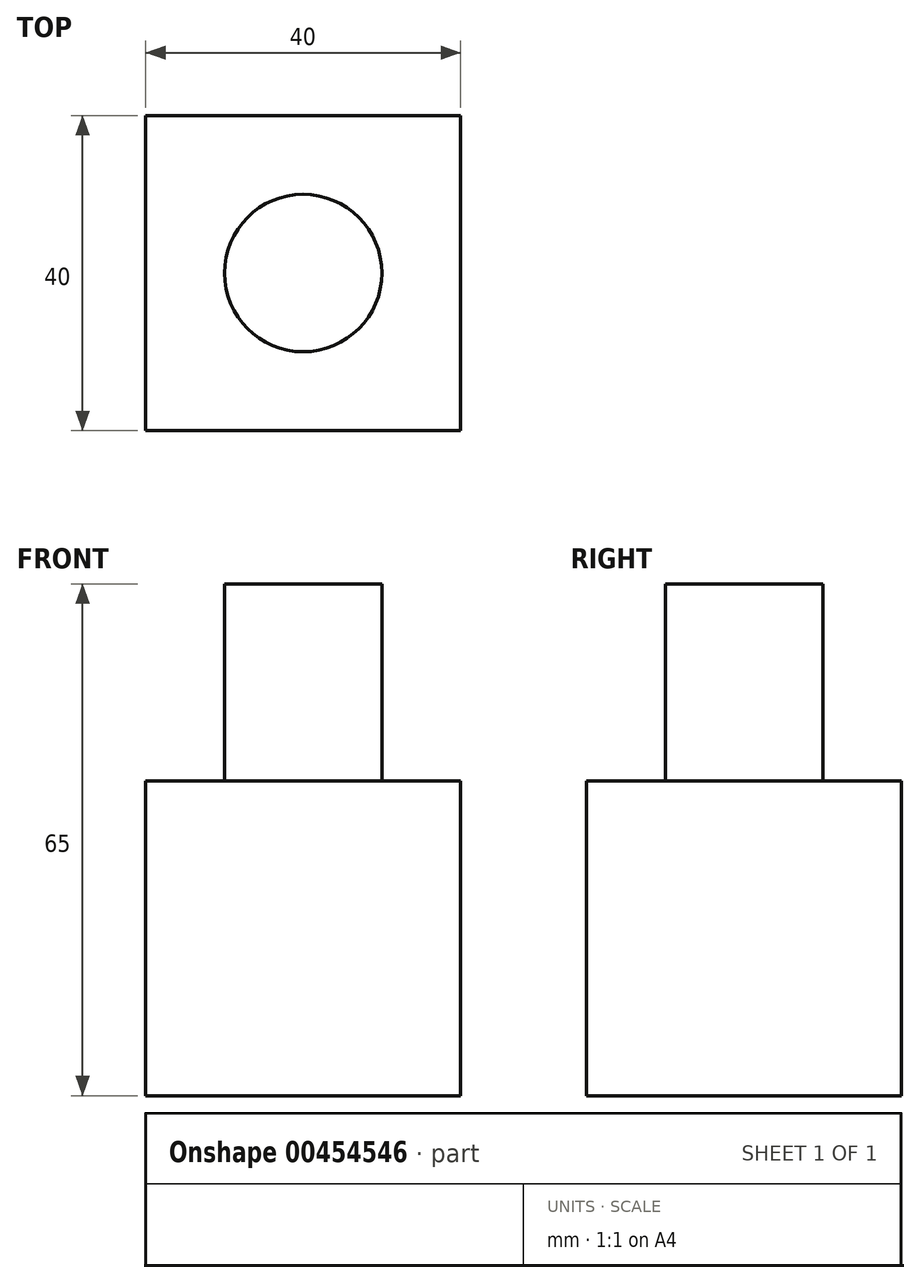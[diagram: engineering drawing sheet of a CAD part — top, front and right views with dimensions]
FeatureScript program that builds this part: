
annotation { "Feature Type Name" : "Feature", "Feature Type Description" : "" }
export const myFeature = defineFeature(function(context is Context, id is Id, definition is map)
    precondition{}
    {
        {
            var Q0;
            Q0=qCreatedBy(makeId("Top.planeOp"),FACE);
            var sketch = newSketch(context, id + "F0", { "sketchPlane" : qUnion([Q0])});
            skLineSegment(sketch, "E0.bottom", {"start": v(-384.05, 0) * mm, "end": v(-344.05, 0) * mm});
            skLineSegment(sketch, "E0.top", {"start": v(-384.05, 40) * mm, "end": v(-344.05, 40) * mm});
            skLineSegment(sketch, "E0.left", {"start": v(-384.05, 0) * mm, "end": v(-384.05, 40) * mm});
            skLineSegment(sketch, "E0.right", {"start": v(-344.05, 0) * mm, "end": v(-344.05, 40) * mm});
            skSolve(sketch);
        }
        {
            var Q0;
            Q0=makeQuery(id+"F0.imprint","IMPRINT",FACE,{"disambiguationData":[TD([[makeQuery(id+"F0.imprint","IMPRINT",EDGE,{"derivedFrom":sQuery(id+"F0.wireOp",EDGE,"E0.bottom")}),1.0]])]});
            extrude(context, id + "F1", {"entities" : qUnion([Q0]), "depth" : 65 * mm});
        }
        {
            var Q0;
            Q0=makeQuery(id+"F1.opExtrude","CAP_FACE",FACE,{"disambiguationData":[OSD([sQuery(id+"F0.wireOp",EDGE,"E0.bottom"),sQuery(id+"F0.wireOp",EDGE,"E0.top"),sQuery(id+"F0.wireOp",EDGE,"E0.left"),sQuery(id+"F0.wireOp",EDGE,"E0.right")])],"isStart":false});
            var sketch = newSketch(context, id + "F2", { "sketchPlane" : qUnion([Q0])});
            skLineSegment(sketch, "E1", {"start": v(-344.05, 0) * mm, "end": v(-384.05, 40) * mm});
            skCircle(sketch, "E2", {"center": v(-364.05, 20) * mm, "radius": 10 * mm});
            skSolve(sketch);
        }
        {
            var Q0;
            {var subQ0=sQuery(id+"F2.wireOp",EDGE,"E2");var subQ1=sQuery(id+"F2.wireOp",EDGE,"E1");var subQ2=makeQuery(id+"F2.imprint","INTERSECT",VERTEX,{"disambiguationData":[OD(0.0)],"derivedFrom":[subQ1,subQ0]});Q0=makeQuery(id+"F2.imprint","IMPRINT",FACE,{"disambiguationData":[TD([[makeQuery(id+"F2.imprint","IMPRINT",EDGE,{"disambiguationData":[TD([[subQ2,-1.0]])],"derivedFrom":subQ1}),-1.0]])]});}
            var Q1;
            {var subQ0=sQuery(id+"F2.wireOp",EDGE,"E2");var subQ1=sQuery(id+"F2.wireOp",EDGE,"E1");var subQ2=makeQuery(id+"F2.imprint","INTERSECT",VERTEX,{"disambiguationData":[OD(0.0)],"derivedFrom":[subQ1,subQ0]});Q1=makeQuery(id+"F2.imprint","IMPRINT",FACE,{"disambiguationData":[TD([[makeQuery(id+"F2.imprint","IMPRINT",EDGE,{"disambiguationData":[TD([[subQ2,-1.0]])],"derivedFrom":subQ1}),1.0]])]});}
            var Q2;
            Q2=sQuery(id+"F2.wireOp",EDGE,"E2");
            extrude(context, id + "F3", {"entities" : qUnion([Q0, Q1]), "operationType" : NewBodyOperationType.REMOVE, "surfaceEntities" : qUnion([Q2]), "oppositeDirection" : true, "depth" : 25 * mm});
        }
    });
